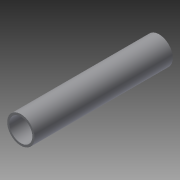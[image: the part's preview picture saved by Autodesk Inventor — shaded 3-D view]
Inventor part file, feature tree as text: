
AUTODESK INVENTOR PART (.ipt)
format: ipt  version: 2015 (Build 190159000, 159)  size: 75,776 bytes
history: native  units: in
note: dims shown in document units (in); Inventor stores cm internally (conversion verified against a paired STEP export)
features: extrude x1, sketch x1
ambient origin geometry x8: Origin, YZ Plane, XZ Plane, XY Plane, X Axis, Y Axis, Z Axis, Center Point
bodies: Solid1 (feature_tree)
feature tree (2):
  extrude  "Extrusion1"  Depth=12.0in
  sketch  "Sketch1"  dims[d0=2.0in d1=2.375in d2=12.0in d3=0.0in]
